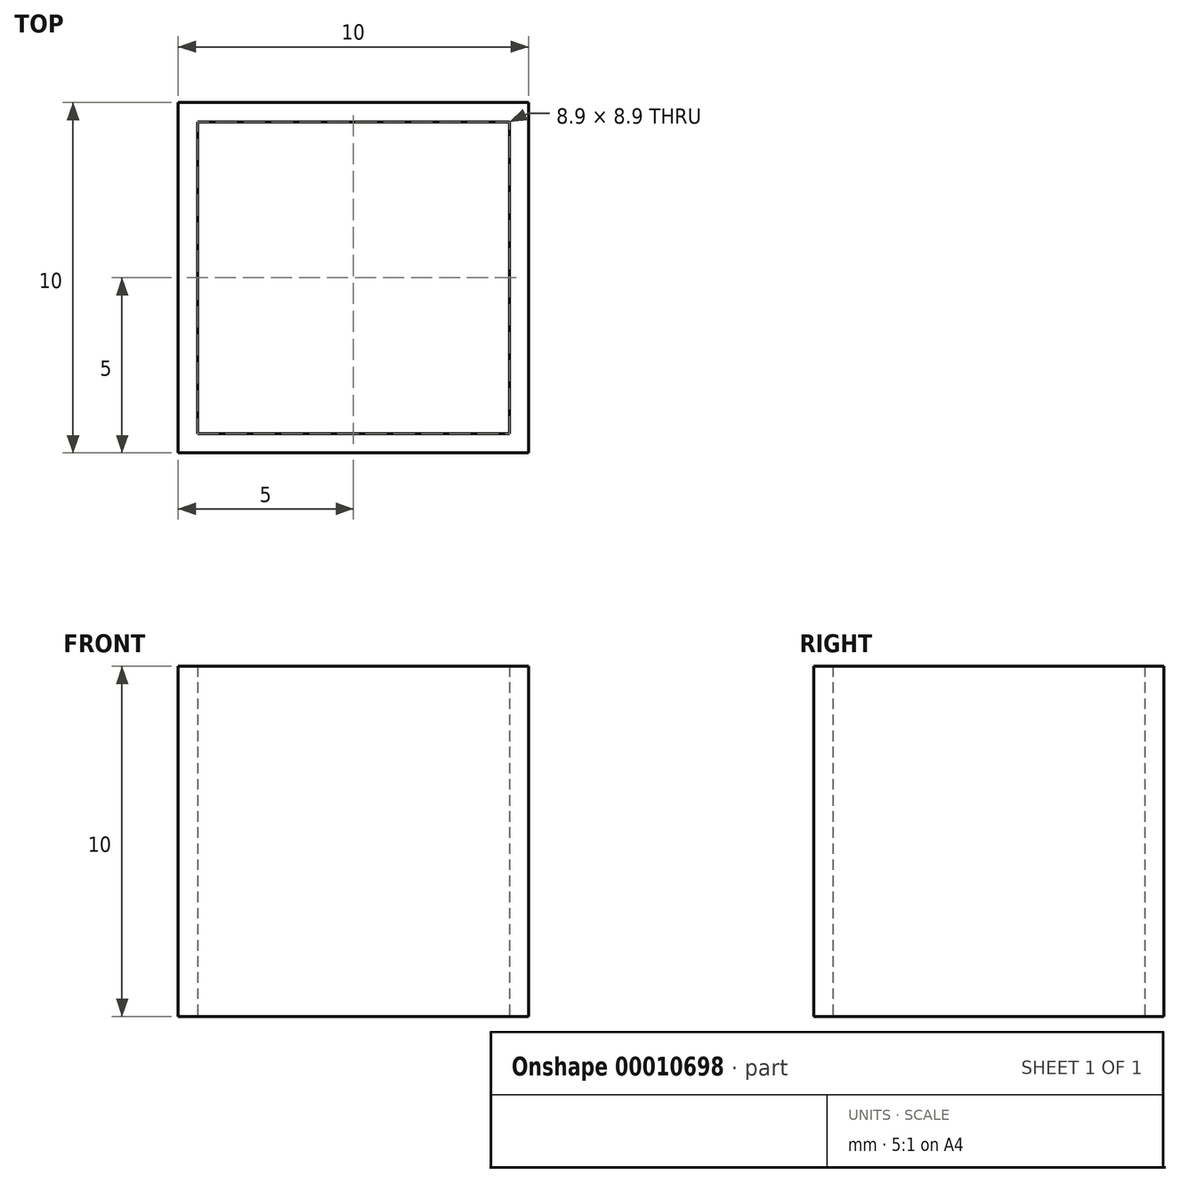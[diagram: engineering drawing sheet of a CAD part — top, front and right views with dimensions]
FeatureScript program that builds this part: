
annotation { "Feature Type Name" : "Feature", "Feature Type Description" : "" }
export const myFeature = defineFeature(function(context is Context, id is Id, definition is map)
    precondition{}
    {
        {
            var Q0;
            Q0=qCreatedBy(makeId("Top.planeOp"),FACE);
            var sketch = newSketch(context, id + "F1", { "sketchPlane" : qUnion([Q0])});
            skLineSegment(sketch, "E0.rect.bottom", {"start": v(4.45, 4.45) * mm, "end": v(-4.45, 4.45) * mm});
            skLineSegment(sketch, "E0.rect.top", {"start": v(4.45, -4.45) * mm, "end": v(-4.45, -4.45) * mm});
            skLineSegment(sketch, "E0.rect.left", {"start": v(4.45, 4.45) * mm, "end": v(4.45, -4.45) * mm});
            skLineSegment(sketch, "E0.rect.right", {"start": v(-4.45, 4.45) * mm, "end": v(-4.45, -4.45) * mm});
            skPoint(sketch, "E0.rect.middle", {"position": v(0, 0) * mm});
            skLineSegment(sketch, "E1.rect.bottom", {"start": v(5, 5) * mm, "end": v(-5, 5) * mm});
            skLineSegment(sketch, "E1.rect.top", {"start": v(5, -5) * mm, "end": v(-5, -5) * mm});
            skLineSegment(sketch, "E1.rect.left", {"start": v(5, 5) * mm, "end": v(5, -5) * mm});
            skLineSegment(sketch, "E1.rect.right", {"start": v(-5, 5) * mm, "end": v(-5, -5) * mm});
            skSolve(sketch);
        }
        {
            var Q0;
            Q0=makeQuery(id+"F1.imprint","IMPRINT",FACE,{"disambiguationData":[TD([[makeQuery(id+"F1.imprint","IMPRINT",EDGE,{"derivedFrom":sQuery(id+"F1.wireOp",EDGE,"E0.rect.bottom")}),-1.0]])]});
            extrude(context, id + "F0", {"entities" : qUnion([Q0]), "depth" : 10 * mm});
        }
    });
